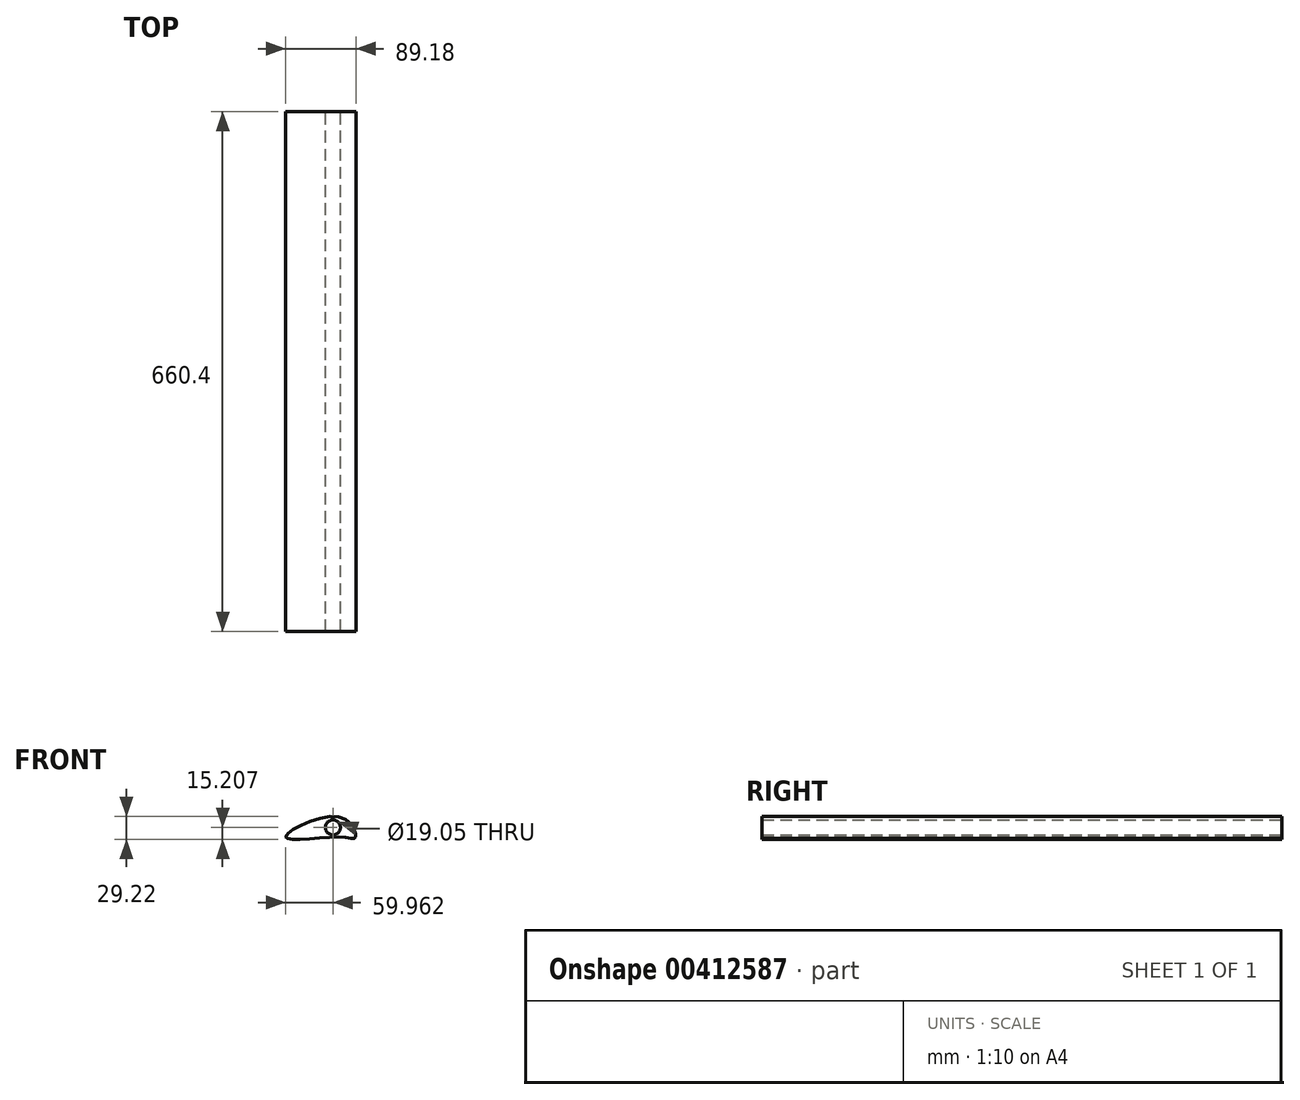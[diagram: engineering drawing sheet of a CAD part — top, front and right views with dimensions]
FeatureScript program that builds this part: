
annotation { "Feature Type Name" : "Feature", "Feature Type Description" : "" }
export const myFeature = defineFeature(function(context is Context, id is Id, definition is map)
    precondition{}
    {
        {
            var Q0;
            Q0=qCreatedBy(makeId("Front.planeOp"),FACE);
            var sketch = newSketch(context, id + "F0", { "sketchPlane" : qUnion([Q0])});
            skFitSpline(sketch, "E0", {"points": [v(34.48, 0) * mm, v(14.25, 25.4) * mm, v(-54.42, 0) * mm, v(15.39, 0) * mm, v(34.48, 0) * mm]});
            skCircle(sketch, "E1", {"center": v(5.52, 12.25) * mm, "radius": 9.53 * mm});
            skSolve(sketch);
        }
        {
            var Q0;
            Q0=qSketchRegion(id+"F0",true);
            extrude(context, id + "F1", {"entities" : qUnion([Q0]), "depth" : 660.4 * mm});
        }
    });
